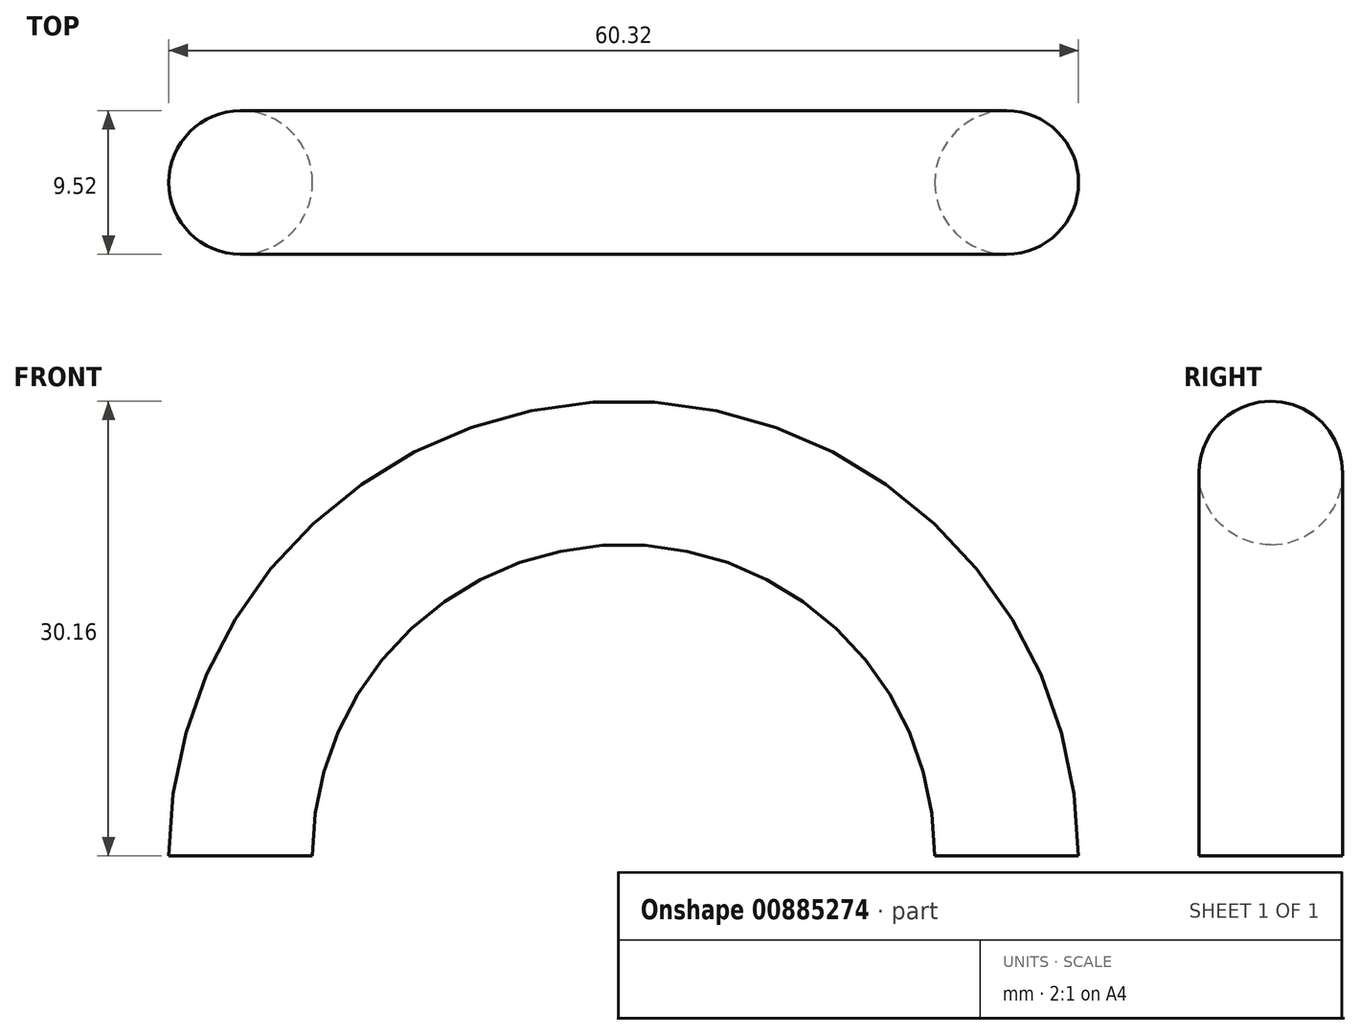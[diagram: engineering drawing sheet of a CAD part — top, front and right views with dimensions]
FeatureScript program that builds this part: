
annotation { "Feature Type Name" : "Feature", "Feature Type Description" : "" }
export const myFeature = defineFeature(function(context is Context, id is Id, definition is map)
    precondition{}
    {
        {
            var Q0;
            Q0=qCreatedBy(makeId("Top.planeOp"),FACE);
            var sketch = newSketch(context, id + "F0", { "sketchPlane" : qUnion([Q0])});
            skCircle(sketch, "E0", {"center": v(-25.4, 0) * mm, "radius": 4.76 * mm});
            skLineSegment(sketch, "E1", {"start": v(0, -62.3) * mm, "end": v(0, 40.18) * mm, "construction": true});
            skSolve(sketch);
        }
        {
            var Q0;
            Q0=makeQuery(id+"F0.imprint","IMPRINT",FACE,{"disambiguationData":[TD([[makeQuery(id+"F0.imprint","IMPRINT",EDGE,{"derivedFrom":sQuery(id+"F0.wireOp",EDGE,"E0")}),1.0]])]});
            var Q1;
            Q1=sQuery(id+"F0.wireOp",EDGE,"E1");
            revolve(context, id + "F1", {"surfaceOperationType" : NewSurfaceOperationType.NEW, "entities" : qUnion([Q0]), "axis" : qUnion([Q1]), "revolveType" : RevolveType.ONE_DIRECTION, "angle" : 180 * degree});
        }
    });
